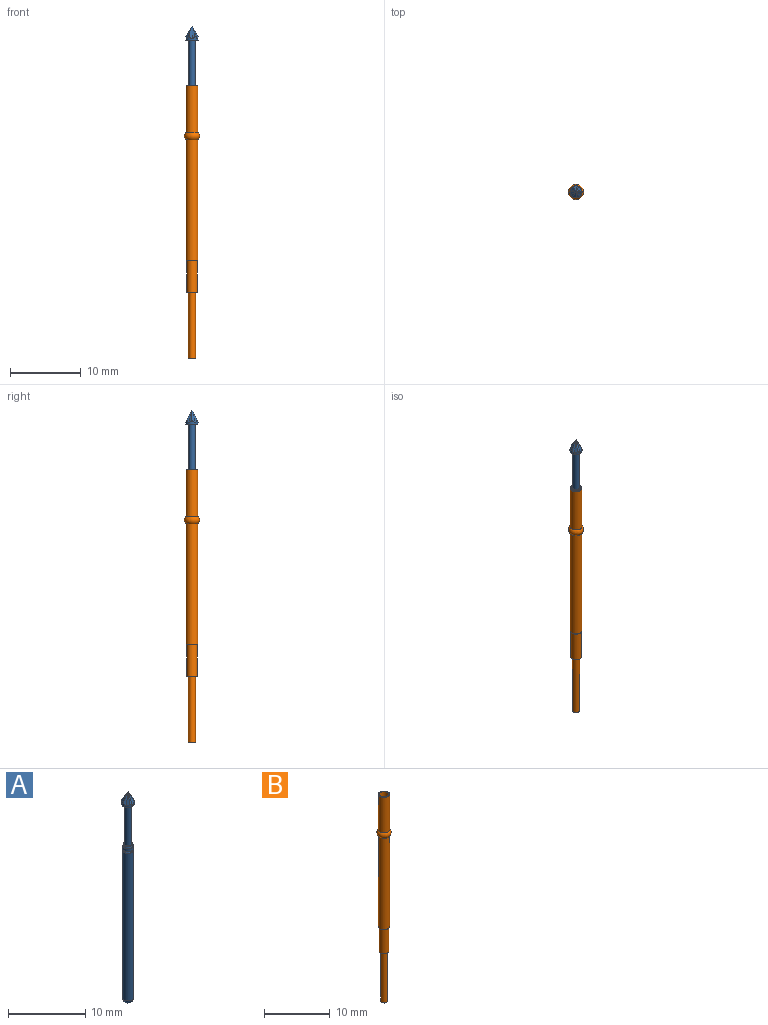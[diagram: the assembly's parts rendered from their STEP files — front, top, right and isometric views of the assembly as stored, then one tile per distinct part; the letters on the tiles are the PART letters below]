
ASSEMBLY  parts=2 mates=1
PART A: 22 faces, bbox 1.7x1.7x33.4 mm
  f0: cylinder r=0.68mm len=23.42mm, axis (0,0,1), area 100.8mm2, adj f1,f2
  f1: torus R=0.74mm, axis (0,0,1), area 1.3mm2, adj f0,f4
  f2: torus R=0.03mm, axis (0,0,-1), area 2.5mm2, adj f0,f3
  f3: plane 0.7x0.7mm, normal (0,0,-1), area 0.4mm2, adj f2
  f4: cylinder r=0.68mm len=1.37mm, axis (0,0,1), area 2mm2, adj f1,f5
  f5: torus R=1.06mm, axis (0,0,1), area 1.2mm2, adj f4,f6
  f6: plane 1.22x1.22mm, normal (0,0,1), area 0.5mm2, adj f5,f7
  f7: cylinder r=0.45mm len=6.4mm, axis (0,0,1), area 18.1mm2, adj f6,f8
  f8: plane 1.7x1.7mm, normal (0,0,-1), area 1.6mm2, adj f7,f9
  f9: cylinder r=0.85mm len=1.7mm, axis (0,0,-1), area 1.7mm2, adj f8,f10,f11,f12,f13,f14,f15,f16
  f10: plane 1.8x0.85mm, normal (0.09,0.9,0.43), area 0.4mm2, adj f9,f11,f21
  f11: plane 1.8x0.85mm, normal (-0.09,0.9,0.43), area 0.4mm2, adj f9,f10,f12
  f12: plane 1.8x0.74mm, normal (0.82,0.37,0.43), area 0.4mm2, adj f9,f11,f13
  f13: plane 1.8x0.85mm, normal (0.74,0.53,0.43), area 0.4mm2, adj f9,f12,f14
  f14: plane 1.8x0.85mm, normal (0.74,-0.53,0.43), area 0.4mm2, adj f9,f13,f15
  f15: plane 1.8x0.74mm, normal (0.82,-0.37,0.43), area 0.4mm2, adj f9,f14,f16
  f16: plane 1.8x0.85mm, normal (-0.09,-0.9,0.43), area 0.4mm2, adj f9,f15,f17
  f17: plane 1.8x0.85mm, normal (0.09,-0.9,0.43), area 0.4mm2, adj f9,f16,f18
  f18: plane 1.8x0.74mm, normal (-0.82,-0.37,0.43), area 0.4mm2, adj f9,f17,f19
  f19: plane 1.8x0.85mm, normal (-0.74,-0.53,0.43), area 0.4mm2, adj f9,f18,f20
  f20: plane 1.8x0.85mm, normal (-0.74,0.53,0.43), area 0.4mm2, adj f9,f19,f21
  f21: plane 1.8x0.74mm, normal (-0.82,0.37,0.43), area 0.4mm2, adj f9,f10,f20
PART B: 11 faces, bbox 1.9x1.7x38.5 mm
  f0: cylinder r=0.84mm len=17.02mm, axis (0,0,1), area 89.8mm2, adj f1,f8
  f1: cone r=0.84mm half-angle=45deg, axis (0,0,1), area 0.7mm2, adj f0,f2
  f2: cylinder r=0.73mm len=4.47mm, axis (0,0,1), area 20.6mm2, adj f1,f3
  f3: plane 1.47x1.47mm, normal (0,0,-1), area 0.9mm2, adj f2,f4
  f4: cylinder r=0.5mm len=9.29mm, axis (0,0,1), area 29.2mm2, adj f3,f5
  f5: plane 1x1mm, normal (0,0,-1), area 0.8mm2, adj f4
  f6: plane 1.68x1.68mm, normal (0,0,1), area 0.7mm2, adj f7,f9
  f7: cylinder r=0.84mm len=6.62mm, axis (0,0,1), area 34.9mm2, adj f6,f8
  f8: torus R=0.41mm, axis (0,0,1), area 7.1mm2, adj f0,f7
  f9: cylinder r=0.69mm len=24.1mm, axis (0,0,1), area 103.8mm2, adj f6,f10
  f10: plane 1.37x1.37mm, normal (0,0,1), area 1.5mm2, adj f9
PLACE A t=(-0.02,0,25.75)mm
PLACE B t=(-0.02,0,-4.08)mm
MATE slider A.f0 <-> B.f9  axis (0,0,1) through (-0.02,0,6.63)mm
